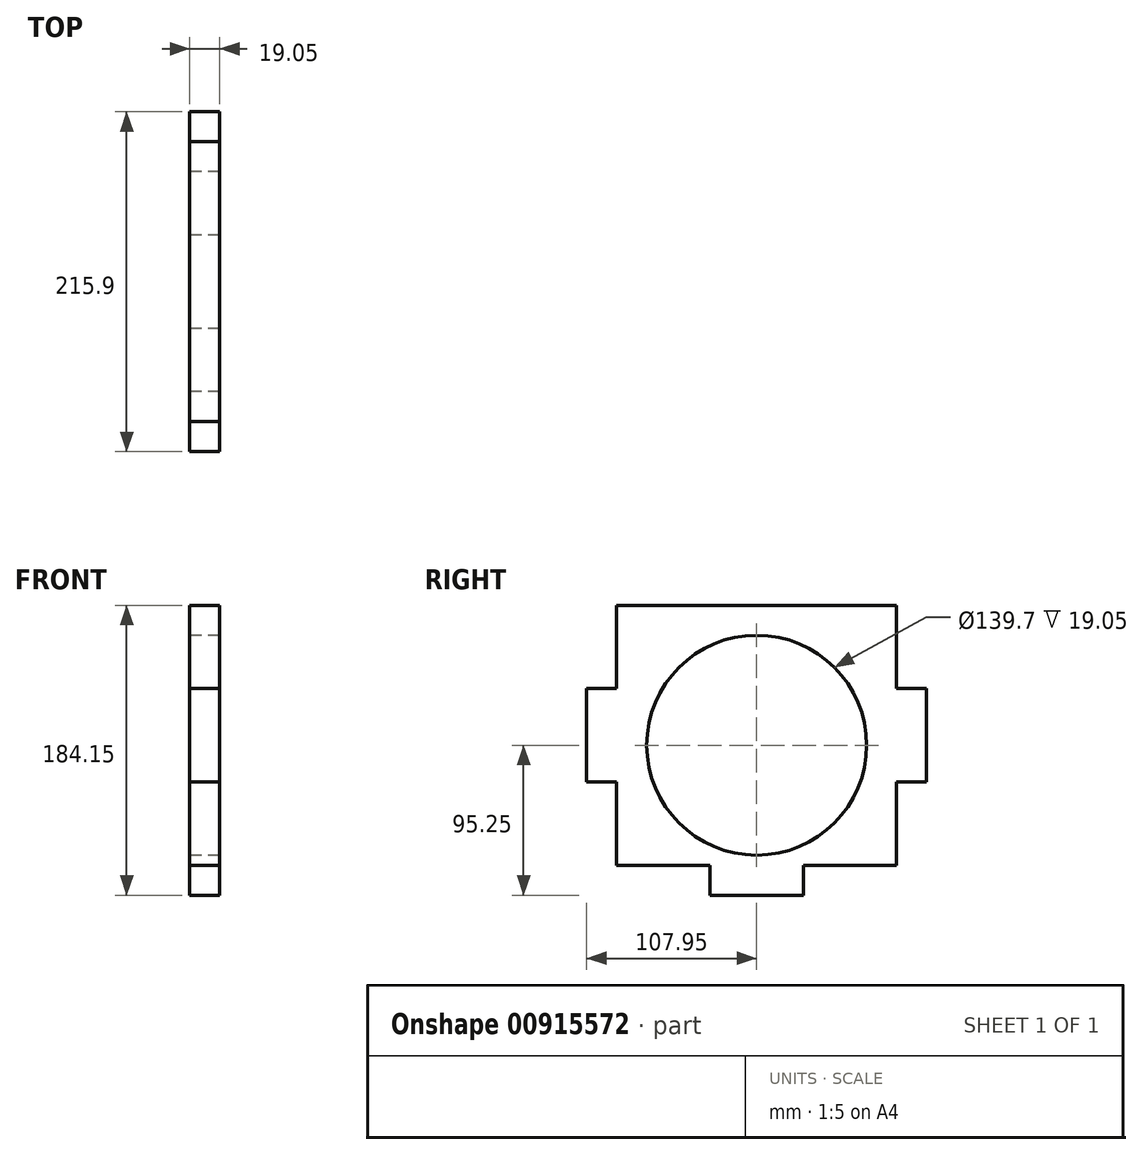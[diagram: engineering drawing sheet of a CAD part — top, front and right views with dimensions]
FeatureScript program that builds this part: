
annotation { "Feature Type Name" : "Feature", "Feature Type Description" : "" }
export const myFeature = defineFeature(function(context is Context, id is Id, definition is map)
    precondition{}
    {
        {
            var Q0;
            Q0=qCreatedBy(makeId("Right.planeOp"),FACE);
            var sketch = newSketch(context, id + "F0", { "sketchPlane" : qUnion([Q0])});
            skLineSegment(sketch, "E0.bottom", {"start": v(-88.9, 82.55) * mm, "end": v(88.9, 82.55) * mm});
            skPoint(sketch, "E0.middle", {"position": v(0, 0) * mm});
            skLineSegment(sketch, "E1", {"start": v(0, -101.6) * mm, "end": v(29.63, -101.6) * mm});
            skLineSegment(sketch, "E2", {"start": v(0, -101.6) * mm, "end": v(-29.63, -101.6) * mm});
            skLineSegment(sketch, "E3", {"start": v(-29.63, -101.6) * mm, "end": v(-29.63, -82.55) * mm});
            skLineSegment(sketch, "E4.top", {"start": v(-29.63, -101.6) * mm, "end": v(29.63, -101.6) * mm});
            skLineSegment(sketch, "E4.left", {"start": v(-29.63, -82.55) * mm, "end": v(-29.63, -101.6) * mm});
            skLineSegment(sketch, "E4.right", {"start": v(29.63, -82.55) * mm, "end": v(29.63, -101.6) * mm});
            skLineSegment(sketch, "E5", {"start": v(88.9, -82.55) * mm, "end": v(29.63, -82.55) * mm});
            skLineSegment(sketch, "E6", {"start": v(-29.63, -82.55) * mm, "end": v(-88.9, -82.55) * mm});
            skLineSegment(sketch, "E7", {"start": v(-107.95, 0) * mm, "end": v(-107.95, 29.63) * mm});
            skLineSegment(sketch, "E8", {"start": v(-107.95, 0) * mm, "end": v(-107.95, -29.63) * mm});
            skLineSegment(sketch, "E9", {"start": v(-107.95, -29.63) * mm, "end": v(-88.9, -29.63) * mm});
            skLineSegment(sketch, "E10.bottom", {"start": v(-88.9, -29.63) * mm, "end": v(-107.95, -29.63) * mm});
            skLineSegment(sketch, "E10.top", {"start": v(-88.9, 29.63) * mm, "end": v(-107.95, 29.63) * mm});
            skLineSegment(sketch, "E10.right", {"start": v(-107.95, -29.63) * mm, "end": v(-107.95, 29.63) * mm});
            skLineSegment(sketch, "E11", {"start": v(-88.9, 29.63) * mm, "end": v(-88.9, 82.55) * mm});
            skLineSegment(sketch, "E12", {"start": v(-88.9, -29.63) * mm, "end": v(-88.9, -82.55) * mm});
            skLineSegment(sketch, "E13", {"start": v(107.95, 0) * mm, "end": v(107.95, 29.63) * mm});
            skLineSegment(sketch, "E14", {"start": v(107.95, 0) * mm, "end": v(107.95, -29.63) * mm});
            skLineSegment(sketch, "E15", {"start": v(107.95, -29.63) * mm, "end": v(88.9, -29.63) * mm});
            skLineSegment(sketch, "E16.bottom", {"start": v(88.9, -29.63) * mm, "end": v(107.95, -29.63) * mm});
            skLineSegment(sketch, "E16.top", {"start": v(88.9, 29.63) * mm, "end": v(107.95, 29.63) * mm});
            skLineSegment(sketch, "E16.right", {"start": v(107.95, -29.63) * mm, "end": v(107.95, 29.63) * mm});
            skLineSegment(sketch, "E17", {"start": v(88.9, -82.55) * mm, "end": v(88.9, -29.63) * mm});
            skLineSegment(sketch, "E18", {"start": v(88.9, 29.63) * mm, "end": v(88.9, 82.55) * mm});
            skCircle(sketch, "E19", {"center": v(0, -6.35) * mm, "radius": 69.85 * mm});
            skSolve(sketch);
        }
        {
            var Q0;
            Q0=makeQuery(id+"F0.imprint","IMPRINT",FACE,{"disambiguationData":[TD([[makeQuery(id+"F0.imprint","IMPRINT",EDGE,{"derivedFrom":sQuery(id+"F0.wireOp",EDGE,"E0.bottom")}),-1.0]])]});
            extrude(context, id + "F1", {"entities" : qUnion([Q0]), "depth" : 19.05 * mm, "offsetDistance" : 25.4 * mm});
        }
    });
